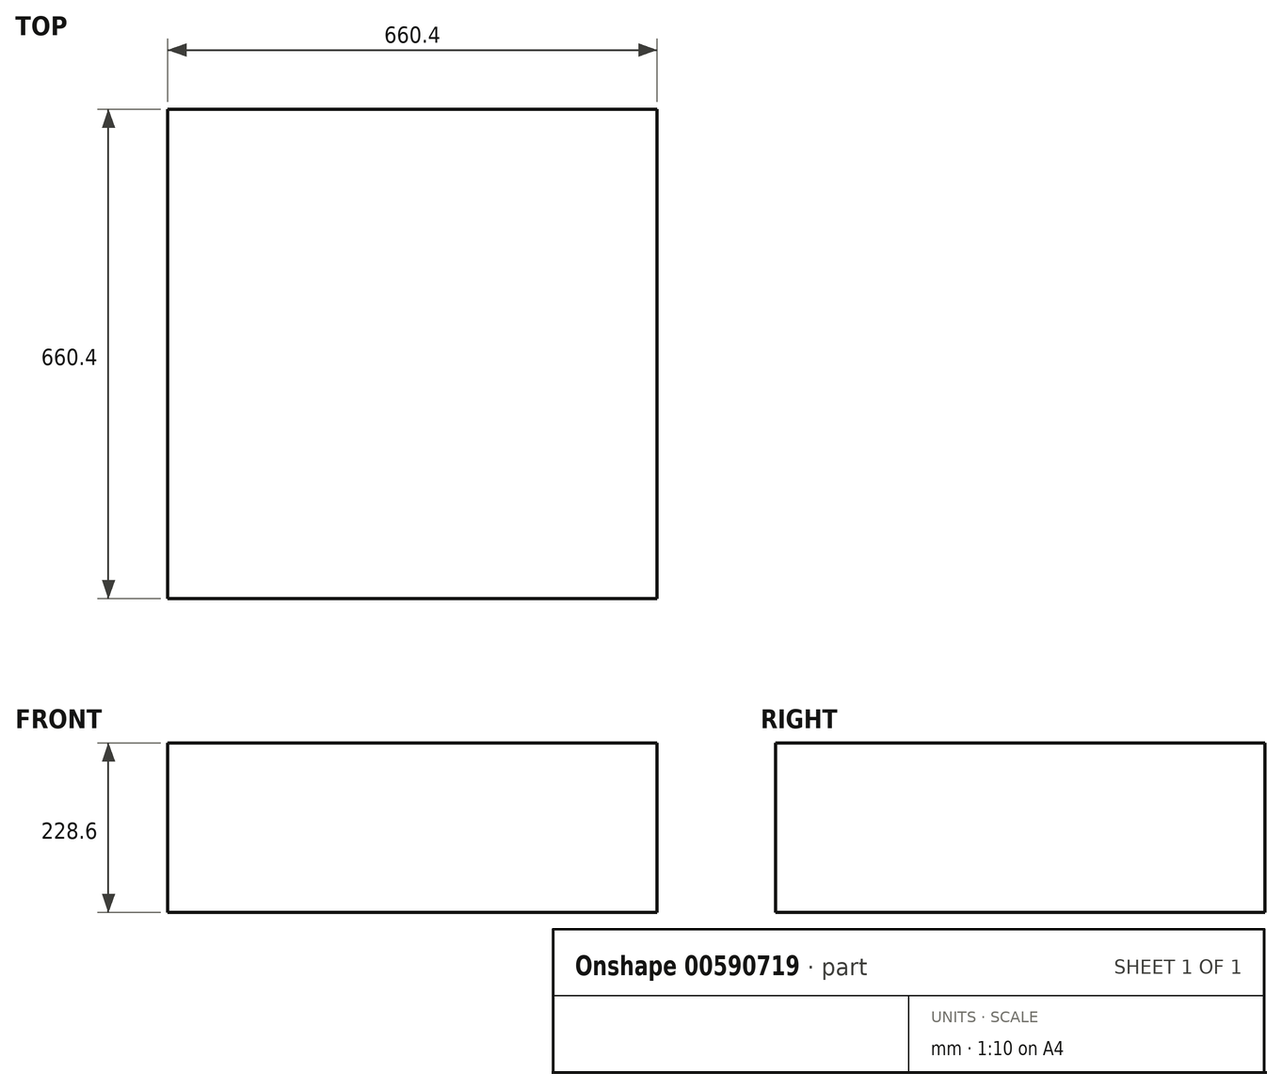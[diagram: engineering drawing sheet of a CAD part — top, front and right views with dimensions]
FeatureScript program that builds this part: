
annotation { "Feature Type Name" : "Feature", "Feature Type Description" : "" }
export const myFeature = defineFeature(function(context is Context, id is Id, definition is map)
    precondition{}
    {
        {
            var Q0;
            Q0=qCreatedBy(makeId("Top.planeOp"),FACE);
            var sketch = newSketch(context, id + "F0", { "sketchPlane" : qUnion([Q0])});
            skLineSegment(sketch, "E0.bottom", {"start": v(330.2, 330.2) * mm, "end": v(-330.2, 330.2) * mm});
            skLineSegment(sketch, "E0.top", {"start": v(330.2, -330.2) * mm, "end": v(-330.2, -330.2) * mm});
            skLineSegment(sketch, "E0.left", {"start": v(330.2, 330.2) * mm, "end": v(330.2, -330.2) * mm});
            skLineSegment(sketch, "E0.right", {"start": v(-330.2, 330.2) * mm, "end": v(-330.2, -330.2) * mm});
            skPoint(sketch, "E0.middle", {"position": v(0, 0) * mm});
            skSolve(sketch);
        }
        {
            var Q0;
            Q0=makeQuery(id+"F0.imprint","IMPRINT",FACE,{"disambiguationData":[TD([[makeQuery(id+"F0.imprint","IMPRINT",EDGE,{"derivedFrom":sQuery(id+"F0.wireOp",EDGE,"E0.bottom")}),1.0]])]});
            extrude(context, id + "F1", {"entities" : qUnion([Q0]), "depth" : 228.6 * mm, "offsetDistance" : 25.4 * mm});
        }
    });
